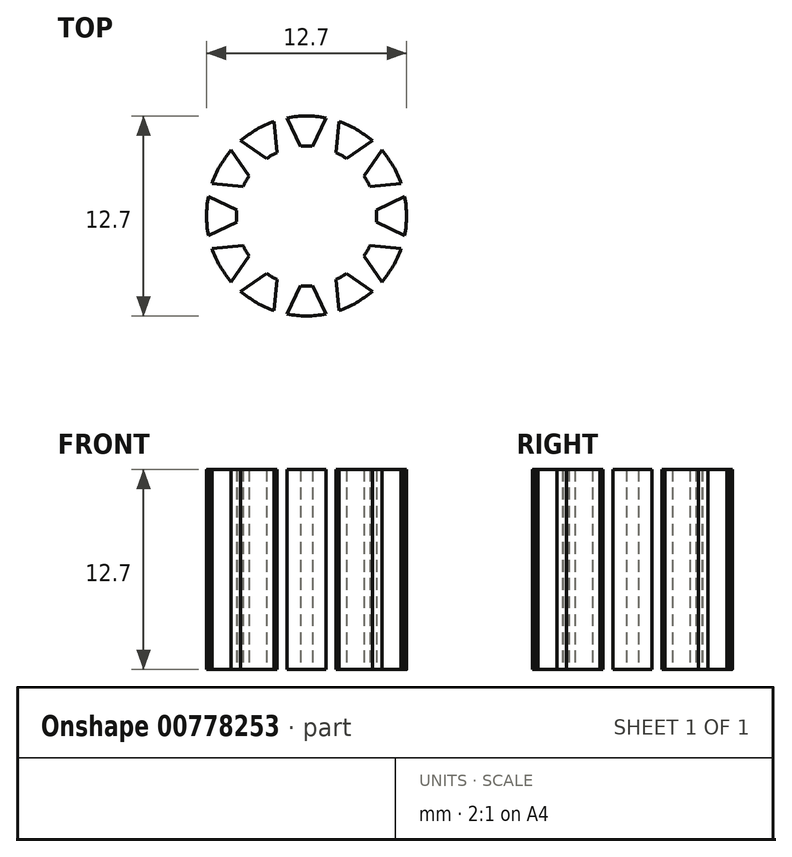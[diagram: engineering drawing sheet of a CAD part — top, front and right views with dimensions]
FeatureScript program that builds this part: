
annotation { "Feature Type Name" : "Feature", "Feature Type Description" : "" }
export const myFeature = defineFeature(function(context is Context, id is Id, definition is map)
    precondition{}
    {
        {
            var Q0;
            Q0=qCreatedBy(makeId("Top.planeOp"),FACE);
            var sketch = newSketch(context, id + "F0", { "sketchPlane" : qUnion([Q0])});
            skCircle(sketch, "E0", {"center": v(0, 0) * mm, "radius": 3.18 * mm});
            skCircle(sketch, "E1", {"center": v(0, 0) * mm, "radius": 6.35 * mm});
            skSolve(sketch);
        }
        {
            var Q0;
            Q0=makeQuery(id+"F0.imprint","IMPRINT",FACE,{"disambiguationData":[TD([[makeQuery(id+"F0.imprint","IMPRINT",EDGE,{"derivedFrom":sQuery(id+"F0.wireOp",EDGE,"E0")}),-1.0]])]});
            extrude(context, id + "F1", {"entities" : qUnion([Q0]), "depth" : 12.7 * mm, "offsetDistance" : 25.4 * mm});
        }
        {
            var Q0;
            Q0=qCreatedBy(makeId("Top.planeOp"),FACE);
            var sketch = newSketch(context, id + "F2", { "sketchPlane" : qUnion([Q0])});
            skLineSegment(sketch, "E2", {"start": v(0, 0) * mm, "end": v(-7.19, 0) * mm, "construction": true});
            skLineSegment(sketch, "E3", {"start": v(0, 0) * mm, "end": v(-6.75, 3.9) * mm, "construction": true});
            skArc(sketch, "E4", {"start": v(-4.45, 0) * mm, "mid": v(-4.44, 0.2) * mm, "end": v(-4.43, 0.39) * mm});
            skArc(sketch, "E5", {"start": v(-3.85, 2.22) * mm, "mid": v(-3.94, 2.05) * mm, "end": v(-4.03, 1.88) * mm});
            skLineSegment(sketch, "E6", {"start": v(0, 0) * mm, "end": v(-4.43, 0.39) * mm, "construction": true});
            skLineSegment(sketch, "E7", {"start": v(0, 0) * mm, "end": v(-4.03, 1.88) * mm, "construction": true});
            skCircle(sketch, "E8.0", {"center": v(0, 0) * mm, "radius": 6.35 * mm, "construction": true});
            skLineSegment(sketch, "E9", {"start": v(-4.43, 0.39) * mm, "end": v(-6.23, 1.23) * mm});
            skLineSegment(sketch, "E10", {"start": v(-4.03, 1.88) * mm, "end": v(-6, 2.05) * mm});
            skArc(sketch, "E11", {"start": v(-6, 2.05) * mm, "mid": v(-6.13, 1.64) * mm, "end": v(-6.23, 1.23) * mm});
            skLineSegment(sketch, "E12.1.0", {"start": v(-4.03, -1.88) * mm, "end": v(-6, -2.05) * mm});
            skArc(sketch, "E12.1.1", {"start": v(-3.85, -2.22) * mm, "mid": v(-3.94, -2.05) * mm, "end": v(-4.03, -1.88) * mm});
            skArc(sketch, "E12.1.2", {"start": v(-4.45, 0) * mm, "mid": v(-4.44, -0.2) * mm, "end": v(-4.43, -0.39) * mm});
            skLineSegment(sketch, "E12.1.3", {"start": v(-4.43, -0.39) * mm, "end": v(-6.23, -1.23) * mm});
            skArc(sketch, "E12.1.4", {"start": v(-6.23, -1.23) * mm, "mid": v(-6.13, -1.64) * mm, "end": v(-6, -2.05) * mm});
            skLineSegment(sketch, "E12.2.0", {"start": v(-2.55, -3.64) * mm, "end": v(-4.18, -4.78) * mm});
            skArc(sketch, "E12.2.1", {"start": v(-2.22, -3.85) * mm, "mid": v(-2.39, -3.75) * mm, "end": v(-2.55, -3.64) * mm});
            skArc(sketch, "E12.2.2", {"start": v(-3.85, -2.22) * mm, "mid": v(-3.75, -2.39) * mm, "end": v(-3.64, -2.55) * mm});
            skLineSegment(sketch, "E12.2.3", {"start": v(-3.64, -2.55) * mm, "end": v(-4.78, -4.18) * mm});
            skArc(sketch, "E12.2.4", {"start": v(-4.78, -4.18) * mm, "mid": v(-4.5, -4.5) * mm, "end": v(-4.18, -4.78) * mm});
            skLineSegment(sketch, "E12.3.0", {"start": v(-0.39, -4.43) * mm, "end": v(-1.23, -6.23) * mm});
            skArc(sketch, "E12.3.1", {"start": v(0, -4.45) * mm, "mid": v(-0.2, -4.44) * mm, "end": v(-0.39, -4.43) * mm});
            skArc(sketch, "E12.3.2", {"start": v(-2.22, -3.85) * mm, "mid": v(-2.05, -3.94) * mm, "end": v(-1.88, -4.03) * mm});
            skLineSegment(sketch, "E12.3.3", {"start": v(-1.88, -4.03) * mm, "end": v(-2.05, -6) * mm});
            skArc(sketch, "E12.3.4", {"start": v(-2.05, -6) * mm, "mid": v(-1.64, -6.13) * mm, "end": v(-1.23, -6.23) * mm});
            skLineSegment(sketch, "E12.4.0", {"start": v(1.88, -4.03) * mm, "end": v(2.05, -6) * mm});
            skArc(sketch, "E12.4.1", {"start": v(2.22, -3.85) * mm, "mid": v(2.05, -3.94) * mm, "end": v(1.88, -4.03) * mm});
            skArc(sketch, "E12.4.2", {"start": v(0, -4.45) * mm, "mid": v(0.2, -4.44) * mm, "end": v(0.39, -4.43) * mm});
            skLineSegment(sketch, "E12.4.3", {"start": v(0.39, -4.43) * mm, "end": v(1.23, -6.23) * mm});
            skArc(sketch, "E12.4.4", {"start": v(1.23, -6.23) * mm, "mid": v(1.64, -6.13) * mm, "end": v(2.05, -6) * mm});
            skLineSegment(sketch, "E12.5.0", {"start": v(3.64, -2.55) * mm, "end": v(4.78, -4.18) * mm});
            skArc(sketch, "E12.5.1", {"start": v(3.85, -2.22) * mm, "mid": v(3.75, -2.39) * mm, "end": v(3.64, -2.55) * mm});
            skArc(sketch, "E12.5.2", {"start": v(2.22, -3.85) * mm, "mid": v(2.39, -3.75) * mm, "end": v(2.55, -3.64) * mm});
            skLineSegment(sketch, "E12.5.3", {"start": v(2.55, -3.64) * mm, "end": v(4.18, -4.78) * mm});
            skArc(sketch, "E12.5.4", {"start": v(4.18, -4.78) * mm, "mid": v(4.5, -4.5) * mm, "end": v(4.78, -4.18) * mm});
            skLineSegment(sketch, "E12.6.0", {"start": v(4.43, -0.39) * mm, "end": v(6.23, -1.23) * mm});
            skArc(sketch, "E12.6.1", {"start": v(4.45, 0) * mm, "mid": v(4.44, -0.2) * mm, "end": v(4.43, -0.39) * mm});
            skArc(sketch, "E12.6.2", {"start": v(3.85, -2.22) * mm, "mid": v(3.94, -2.05) * mm, "end": v(4.03, -1.88) * mm});
            skLineSegment(sketch, "E12.6.3", {"start": v(4.03, -1.88) * mm, "end": v(6, -2.05) * mm});
            skArc(sketch, "E12.6.4", {"start": v(6, -2.05) * mm, "mid": v(6.13, -1.64) * mm, "end": v(6.23, -1.23) * mm});
            skLineSegment(sketch, "E12.7.0", {"start": v(4.03, 1.88) * mm, "end": v(6, 2.05) * mm});
            skArc(sketch, "E12.7.1", {"start": v(3.85, 2.22) * mm, "mid": v(3.94, 2.05) * mm, "end": v(4.03, 1.88) * mm});
            skArc(sketch, "E12.7.2", {"start": v(4.45, 0) * mm, "mid": v(4.44, 0.2) * mm, "end": v(4.43, 0.39) * mm});
            skLineSegment(sketch, "E12.7.3", {"start": v(4.43, 0.39) * mm, "end": v(6.23, 1.23) * mm});
            skArc(sketch, "E12.7.4", {"start": v(6.23, 1.23) * mm, "mid": v(6.13, 1.64) * mm, "end": v(6, 2.05) * mm});
            skLineSegment(sketch, "E12.8.0", {"start": v(2.55, 3.64) * mm, "end": v(4.18, 4.78) * mm});
            skArc(sketch, "E12.8.1", {"start": v(2.22, 3.85) * mm, "mid": v(2.39, 3.75) * mm, "end": v(2.55, 3.64) * mm});
            skArc(sketch, "E12.8.2", {"start": v(3.85, 2.22) * mm, "mid": v(3.75, 2.39) * mm, "end": v(3.64, 2.55) * mm});
            skLineSegment(sketch, "E12.8.3", {"start": v(3.64, 2.55) * mm, "end": v(4.78, 4.18) * mm});
            skArc(sketch, "E12.8.4", {"start": v(4.78, 4.18) * mm, "mid": v(4.5, 4.5) * mm, "end": v(4.18, 4.78) * mm});
            skLineSegment(sketch, "E12.9.0", {"start": v(0.39, 4.43) * mm, "end": v(1.23, 6.23) * mm});
            skArc(sketch, "E12.9.1", {"start": v(0, 4.45) * mm, "mid": v(0.2, 4.44) * mm, "end": v(0.39, 4.43) * mm});
            skArc(sketch, "E12.9.2", {"start": v(2.22, 3.85) * mm, "mid": v(2.05, 3.94) * mm, "end": v(1.88, 4.03) * mm});
            skLineSegment(sketch, "E12.9.3", {"start": v(1.88, 4.03) * mm, "end": v(2.05, 6) * mm});
            skArc(sketch, "E12.9.4", {"start": v(2.05, 6) * mm, "mid": v(1.64, 6.13) * mm, "end": v(1.23, 6.23) * mm});
            skLineSegment(sketch, "E12.10.0", {"start": v(-1.88, 4.03) * mm, "end": v(-2.05, 6) * mm});
            skArc(sketch, "E12.10.1", {"start": v(-2.22, 3.85) * mm, "mid": v(-2.05, 3.94) * mm, "end": v(-1.88, 4.03) * mm});
            skArc(sketch, "E12.10.2", {"start": v(0, 4.45) * mm, "mid": v(-0.2, 4.44) * mm, "end": v(-0.39, 4.43) * mm});
            skLineSegment(sketch, "E12.10.3", {"start": v(-0.39, 4.43) * mm, "end": v(-1.23, 6.23) * mm});
            skArc(sketch, "E12.10.4", {"start": v(-1.23, 6.23) * mm, "mid": v(-1.64, 6.13) * mm, "end": v(-2.05, 6) * mm});
            skLineSegment(sketch, "E12.11.0", {"start": v(-3.64, 2.55) * mm, "end": v(-4.78, 4.18) * mm});
            skArc(sketch, "E12.11.1", {"start": v(-3.85, 2.22) * mm, "mid": v(-3.75, 2.39) * mm, "end": v(-3.64, 2.55) * mm});
            skArc(sketch, "E12.11.2", {"start": v(-2.22, 3.85) * mm, "mid": v(-2.39, 3.75) * mm, "end": v(-2.55, 3.64) * mm});
            skLineSegment(sketch, "E12.11.3", {"start": v(-2.55, 3.64) * mm, "end": v(-4.18, 4.78) * mm});
            skArc(sketch, "E12.11.4", {"start": v(-4.18, 4.78) * mm, "mid": v(-4.5, 4.5) * mm, "end": v(-4.78, 4.18) * mm});
            skCircle(sketch, "E13", {"center": v(0, 0) * mm, "radius": 6.7 * mm});
            skSolve(sketch);
        }
        {
            var Q0;
            Q0=makeQuery(id+"F2.imprint","IMPRINT",FACE,{"disambiguationData":[TD([[makeQuery(id+"F2.imprint","IMPRINT",EDGE,{"derivedFrom":sQuery(id+"F2.wireOp",EDGE,"E4")}),1.0]])]});
            var Q1;
            Q1=makeQuery(id+"F1.opExtrude","CAP_FACE",FACE,{"disambiguationData":[OSD([sQuery(id+"F0.wireOp",EDGE,"E0"),sQuery(id+"F0.wireOp",EDGE,"E1")])],"isStart":false});
            extrude(context, id + "F3", {"entities" : qUnion([Q0]), "operationType" : NewBodyOperationType.REMOVE, "endBound" : BoundingType.UP_TO_SURFACE, "depth" : 25.4 * mm, "endBoundEntityFace" : qUnion([Q1]), "offsetDistance" : 25.4 * mm});
        }
    });
